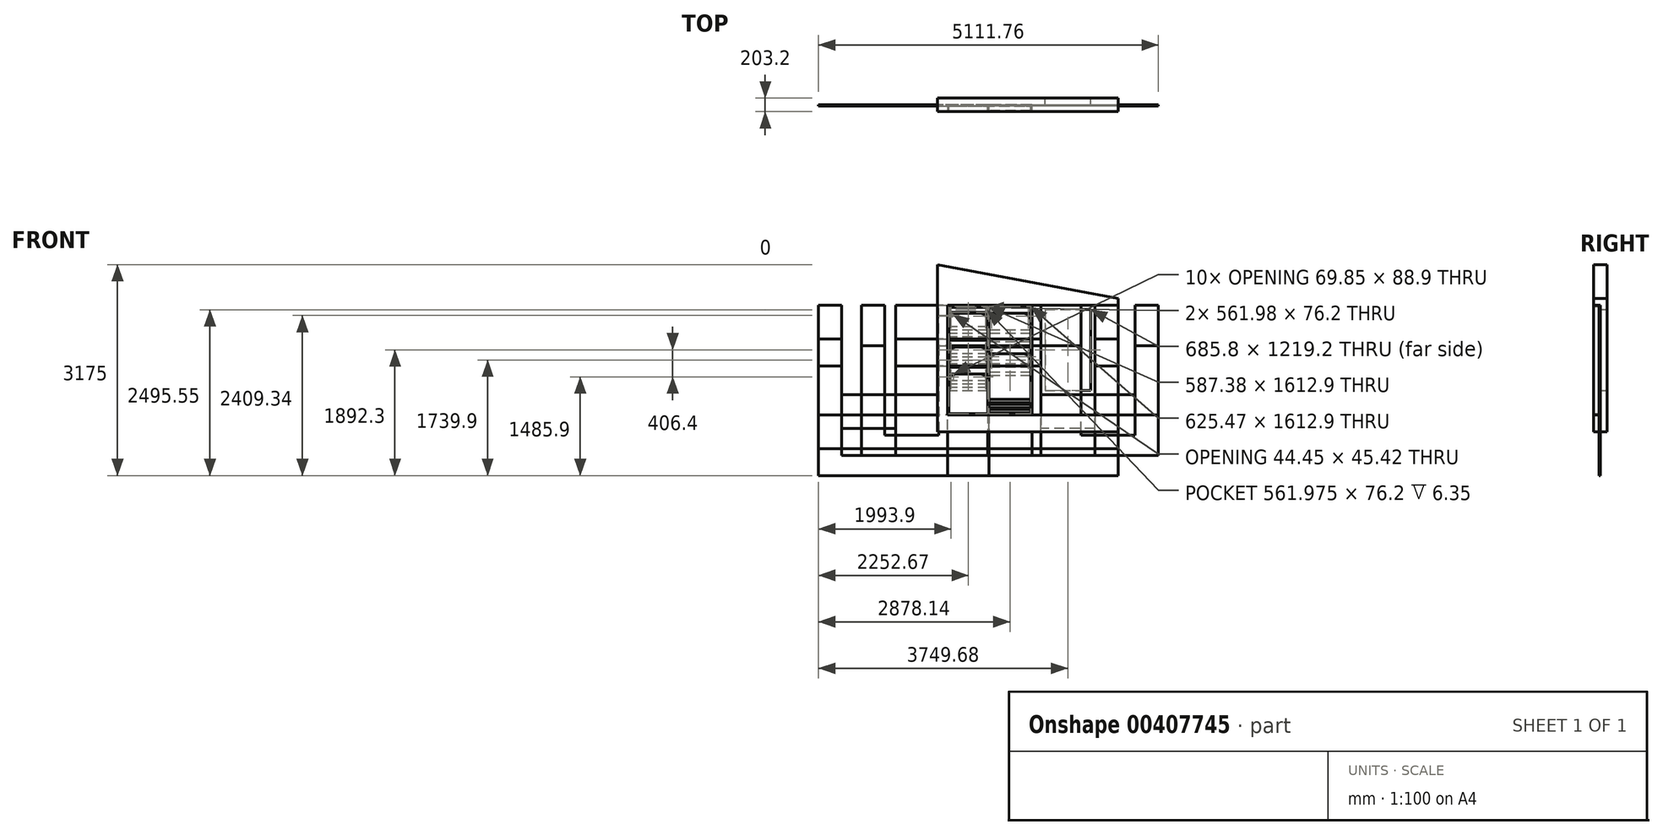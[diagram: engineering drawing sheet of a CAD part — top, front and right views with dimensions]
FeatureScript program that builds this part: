
annotation { "Feature Type Name" : "Feature", "Feature Type Description" : "" }
export const myFeature = defineFeature(function(context is Context, id is Id, definition is map)
    precondition{}
    {
        {
            var Q0;
            Q0=qCreatedBy(makeId("Front.planeOp"),FACE);
            var sketch = newSketch(context, id + "F0", { "sketchPlane" : qUnion([Q0])});
            skLineSegment(sketch, "E0.bottom", {"start": v(0, 0) * mm, "end": v(2717.8, 0) * mm});
            skLineSegment(sketch, "E0.top", {"start": v(0, 2006.6) * mm, "end": v(2717.8, 2006.6) * mm});
            skLineSegment(sketch, "E0.left", {"start": v(0, 0) * mm, "end": v(0, 2006.6) * mm});
            skLineSegment(sketch, "E0.right", {"start": v(2717.8, 0) * mm, "end": v(2717.8, 2006.6) * mm});
            skLineSegment(sketch, "E1.bottom", {"start": v(152.4, 254) * mm, "end": v(2717.8, 254) * mm});
            skLineSegment(sketch, "E1.top", {"start": v(152.4, 1905) * mm, "end": v(2717.8, 1905) * mm});
            skLineSegment(sketch, "E1.left", {"start": v(152.4, 254) * mm, "end": v(152.4, 1905) * mm});
            skLineSegment(sketch, "E1.right", {"start": v(2717.8, 254) * mm, "end": v(2717.8, 1905) * mm});
            skLineSegment(sketch, "E2", {"start": v(2717.8, 2006.6) * mm, "end": v(0, 2514.6) * mm});
            skLineSegment(sketch, "E3", {"start": v(0, 2514.6) * mm, "end": v(0, 2006.6) * mm});
            skSolve(sketch);
        }
        {
            var Q0;
            Q0=makeQuery(id+"F0.imprint","IMPRINT",FACE,{"disambiguationData":[TD([[makeQuery(id+"F0.imprint","IMPRINT",EDGE,{"derivedFrom":sQuery(id+"F0.wireOp",EDGE,"E0.bottom")}),1.0]])]});
            var Q1;
            Q1=makeQuery(id+"F0.imprint","IMPRINT",FACE,{"disambiguationData":[TD([[makeQuery(id+"F0.imprint","IMPRINT",EDGE,{"derivedFrom":sQuery(id+"F0.wireOp",EDGE,"E0.top")}),1.0]])]});
            var Q2;
            Q2=makeQuery(id+"F0.imprint","IMPRINT",FACE,{"disambiguationData":[TD([[makeQuery(id+"F0.imprint","IMPRINT",EDGE,{"derivedFrom":sQuery(id+"F0.wireOp",EDGE,"E1.bottom")}),1.0]])]});
            extrude(context, id + "F1", {"entities" : qUnion([Q0, Q1, Q2]), "oppositeDirection" : true, "depth" : 203.2 * mm});
        }
        {
            var Q0;
            Q0=makeQuery(id+"F0.imprint","IMPRINT",FACE,{"disambiguationData":[TD([[makeQuery(id+"F0.imprint","IMPRINT",EDGE,{"derivedFrom":sQuery(id+"F0.wireOp",EDGE,"E1.bottom")}),1.0]])]});
            extrude(context, id + "F2", {"entities" : qUnion([Q0]), "operationType" : NewBodyOperationType.REMOVE, "oppositeDirection" : true, "depth" : 101.6 * mm});
        }
        {
            var Q0;
            Q0=makeQuery(id+"F2.boolean.opBoolean","COPY",FACE,{"derivedFrom":makeQuery(id+"F2.opExtrude","CAP_FACE",FACE,{"disambiguationData":[OSD([sQuery(id+"F0.wireOp",EDGE,"E1.bottom"),sQuery(id+"F0.wireOp",EDGE,"E1.top"),sQuery(id+"F0.wireOp",EDGE,"E1.left"),sQuery(id+"F0.wireOp",EDGE,"E1.right")])],"isStart":false})});
            var sketch = newSketch(context, id + "F3", { "sketchPlane" : qUnion([Q0])});
            skLineSegment(sketch, "E4.bottom", {"start": v(1555.75, 1905) * mm, "end": v(2368.55, 1905) * mm});
            skLineSegment(sketch, "E4.top", {"start": v(1555.75, 558.8) * mm, "end": v(2368.55, 558.8) * mm});
            skLineSegment(sketch, "E4.left", {"start": v(1555.75, 1905) * mm, "end": v(1555.75, 558.8) * mm});
            skLineSegment(sketch, "E4.right", {"start": v(2368.55, 1905) * mm, "end": v(2368.55, 558.8) * mm});
            skLineSegment(sketch, "E5.0", {"start": v(1619.25, 1841.5) * mm, "end": v(1619.25, 622.3) * mm});
            skLineSegment(sketch, "E5.1", {"start": v(1619.25, 1841.5) * mm, "end": v(2305.05, 1841.5) * mm});
            skLineSegment(sketch, "E5.2", {"start": v(2305.05, 1841.5) * mm, "end": v(2305.05, 622.3) * mm});
            skLineSegment(sketch, "E5.3", {"start": v(1619.25, 622.3) * mm, "end": v(2305.05, 622.3) * mm});
            skSolve(sketch);
        }
        {
            var Q0;
            Q0=makeQuery(id+"F3.imprint","IMPRINT",FACE,{"disambiguationData":[TD([[makeQuery(id+"F3.imprint","IMPRINT",EDGE,{"derivedFrom":sQuery(id+"F3.wireOp",EDGE,"E4.bottom")}),-1.0]])]});
            extrude(context, id + "F4", {"entities" : qUnion([Q0]), "operationType" : NewBodyOperationType.ADD, "depth" : 12.7 * mm});
        }
        {
            var Q0;
            Q0=makeQuery(id+"F3.imprint","IMPRINT",FACE,{"disambiguationData":[TD([[makeQuery(id+"F3.imprint","IMPRINT",EDGE,{"derivedFrom":sQuery(id+"F3.wireOp",EDGE,"E5.0")}),1.0]])]});
            extrude(context, id + "F5", {"entities" : qUnion([Q0]), "operationType" : NewBodyOperationType.REMOVE, "endBound" : BoundingType.THROUGH_ALL, "oppositeDirection" : true, "depth" : 25.4 * mm});
        }
        {
            var Q0;
            {var subQ0=sQuery(id+"F0.wireOp",EDGE,"E1.left");var subQ1=sQuery(id+"F0.wireOp",EDGE,"E1.bottom");var subQ2=sQuery(id+"F0.wireOp",EDGE,"E1.top");var subQ3=sQuery(id+"F0.wireOp",EDGE,"E1.right");Q0=makeQuery(id+"F4.boolean.opBoolean","SPLIT",FACE,{"disambiguationData":[TD([makeQuery(id+"F2.boolean.opBoolean","COPY",FACE,{"derivedFrom":makeQuery(id+"F2.opExtrude","SWEPT_FACE",FACE,{"disambiguationData":[OSD([subQ1])]})})])],"derivedFrom":makeQuery(id+"F2.boolean.opBoolean","COPY",FACE,{"derivedFrom":makeQuery(id+"F2.opExtrude","CAP_FACE",FACE,{"disambiguationData":[OSD([subQ1,subQ2,subQ0,subQ3])],"isStart":false})})});}
            var sketch = newSketch(context, id + "F6", { "sketchPlane" : qUnion([Q0])});
            skLineSegment(sketch, "E6.bottom", {"start": v(152.4, 1905) * mm, "end": v(1422.4, 1905) * mm});
            skLineSegment(sketch, "E6.top", {"start": v(152.4, 254) * mm, "end": v(1422.4, 254) * mm});
            skLineSegment(sketch, "E6.left", {"start": v(152.4, 1905) * mm, "end": v(152.4, 254) * mm});
            skLineSegment(sketch, "E6.right", {"start": v(1422.4, 1905) * mm, "end": v(1422.4, 254) * mm});
            skLineSegment(sketch, "E7.bottom", {"start": v(171.45, 1885.95) * mm, "end": v(758.82, 1885.95) * mm});
            skLineSegment(sketch, "E7.top", {"start": v(171.45, 273.05) * mm, "end": v(758.82, 273.05) * mm});
            skLineSegment(sketch, "E7.left", {"start": v(171.45, 1885.95) * mm, "end": v(171.45, 273.05) * mm});
            skLineSegment(sketch, "E7.right", {"start": v(758.82, 1885.95) * mm, "end": v(758.82, 273.05) * mm});
            skLineSegment(sketch, "E8.bottom", {"start": v(777.87, 1885.95) * mm, "end": v(1403.35, 1885.95) * mm});
            skLineSegment(sketch, "E8.top", {"start": v(777.87, 273.05) * mm, "end": v(1403.35, 273.05) * mm});
            skLineSegment(sketch, "E8.left", {"start": v(777.87, 1885.95) * mm, "end": v(777.87, 273.05) * mm});
            skLineSegment(sketch, "E8.right", {"start": v(1403.35, 1885.95) * mm, "end": v(1403.35, 273.05) * mm});
            skSolve(sketch);
        }
        {
            var Q0;
            Q0=makeQuery(id+"F6.imprint","IMPRINT",FACE,{"disambiguationData":[TD([[makeQuery(id+"F6.imprint","IMPRINT",EDGE,{"derivedFrom":sQuery(id+"F6.wireOp",EDGE,"E6.bottom")}),-1.0]])]});
            extrude(context, id + "F7", {"entities" : qUnion([Q0]), "depth" : 101.6 * mm});
        }
        {
            var Q0;
            Q0=makeQuery(id+"F7.opExtrude","SWEPT_FACE",FACE,{"disambiguationData":[OSD([sQuery(id+"F6.wireOp",EDGE,"E7.left")])]});
            var sketch = newSketch(context, id + "F8", { "sketchPlane" : qUnion([Q0])});
            skLineSegment(sketch, "E9.bottom", {"start": v(101.6, 1885.95) * mm, "end": v(82.55, 1885.95) * mm});
            skLineSegment(sketch, "E9.top", {"start": v(101.6, 1784.35) * mm, "end": v(82.55, 1784.35) * mm});
            skLineSegment(sketch, "E9.left", {"start": v(101.6, 1885.95) * mm, "end": v(101.6, 1784.35) * mm});
            skLineSegment(sketch, "E9.right", {"start": v(82.55, 1885.95) * mm, "end": v(82.55, 1784.35) * mm});
            skSolve(sketch);
        }
        {
            var Q0;
            Q0=makeQuery(id+"F8.imprint","IMPRINT",FACE,{"disambiguationData":[TD([[makeQuery(id+"F8.imprint","IMPRINT",EDGE,{"derivedFrom":sQuery(id+"F8.wireOp",EDGE,"E9.bottom")}),-1.0]])]});
            extrude(context, id + "F9", {"entities" : qUnion([Q0]), "endBound" : BoundingType.UP_TO_NEXT, "depth" : 25.4 * mm});
        }
        {
            var Q0;
            Q0=makeQuery(id+"F9.opExtrude","SWEPT_BODY",BODY,{"disambiguationData":[OSD([sQuery(id+"F8.wireOp",EDGE,"E9.bottom"),sQuery(id+"F8.wireOp",EDGE,"E9.top"),sQuery(id+"F8.wireOp",EDGE,"E9.left"),sQuery(id+"F8.wireOp",EDGE,"E9.right")])]});
            transform(context, id + "F10", {"entities" : qUnion([Q0]), "transformType" : TransformType.TRANSLATION_3D, "dx" : 0 * mm, "dy" : 0 * mm, "dz" : -508 * mm, "makeCopy" : true});
        }
        {
            var Q0;
            Q0=makeQuery(id+"F10.opPattern","COPY",BODY,{"derivedFrom":makeQuery(id+"F9.opExtrude","SWEPT_BODY",BODY,{"disambiguationData":[OSD([sQuery(id+"F8.wireOp",EDGE,"E9.bottom"),sQuery(id+"F8.wireOp",EDGE,"E9.top"),sQuery(id+"F8.wireOp",EDGE,"E9.left"),sQuery(id+"F8.wireOp",EDGE,"E9.right")])]}),"instanceName":"1"});
            transform(context, id + "F11", {"entities" : qUnion([Q0]), "transformType" : TransformType.TRANSLATION_3D, "dx" : 0 * mm, "dy" : 0 * mm, "dz" : -406.4 * mm, "makeCopy" : true});
        }
        {
            var Q0;
            Q0=makeQuery(id+"F7.opExtrude","SWEPT_FACE",FACE,{"disambiguationData":[OSD([sQuery(id+"F6.wireOp",EDGE,"E8.left")])]});
            var sketch = newSketch(context, id + "F12", { "sketchPlane" : qUnion([Q0])});
            skLineSegment(sketch, "E10.bottom", {"start": v(101.6, 1885.95) * mm, "end": v(82.55, 1885.95) * mm});
            skLineSegment(sketch, "E10.top", {"start": v(101.6, 1784.35) * mm, "end": v(82.55, 1784.35) * mm});
            skLineSegment(sketch, "E10.left", {"start": v(101.6, 1885.95) * mm, "end": v(101.6, 1784.35) * mm});
            skLineSegment(sketch, "E10.right", {"start": v(82.55, 1885.95) * mm, "end": v(82.55, 1784.35) * mm});
            skLineSegment(sketch, "E11.0", {"start": v(101.6, 1784.35) * mm, "end": v(82.55, 1784.35) * mm, "construction": true});
            skSolve(sketch);
        }
        {
            var Q0;
            Q0=makeQuery(id+"F12.imprint","IMPRINT",FACE,{"disambiguationData":[TD([[makeQuery(id+"F12.imprint","IMPRINT",EDGE,{"derivedFrom":sQuery(id+"F12.wireOp",EDGE,"E10.bottom")}),-1.0]])]});
            extrude(context, id + "F13", {"entities" : qUnion([Q0]), "endBound" : BoundingType.UP_TO_NEXT, "depth" : 25.4 * mm});
        }
        {
            var Q0;
            Q0=makeQuery(id+"F13.opExtrude","SWEPT_BODY",BODY,{"disambiguationData":[OSD([sQuery(id+"F12.wireOp",EDGE,"E10.bottom"),sQuery(id+"F12.wireOp",EDGE,"E10.top"),sQuery(id+"F12.wireOp",EDGE,"E10.left"),sQuery(id+"F12.wireOp",EDGE,"E10.right")])]});
            transform(context, id + "F14", {"entities" : qUnion([Q0]), "transformType" : TransformType.TRANSLATION_3D, "dx" : 0 * mm, "dy" : 0 * mm, "dz" : -609.6 * mm, "makeCopy" : true});
        }
        {
            var Q0;
            Q0=makeQuery(id+"F7.opExtrude","SWEPT_FACE",FACE,{"disambiguationData":[OSD([sQuery(id+"F6.wireOp",EDGE,"E7.left")])]});
            var sketch = newSketch(context, id + "F15", { "sketchPlane" : qUnion([Q0])});
            skLineSegment(sketch, "E12.0", {"start": v(82.55, 1377.95) * mm, "end": v(101.6, 1377.95) * mm, "construction": true});
            skLineSegment(sketch, "E13.0", {"start": v(101.6, 1885.95) * mm, "end": v(101.6, 273.05) * mm, "construction": true});
            skLineSegment(sketch, "E14.bottom", {"start": v(101.6, 1428.75) * mm, "end": v(88.9, 1428.75) * mm});
            skLineSegment(sketch, "E14.top", {"start": v(101.6, 1479.55) * mm, "end": v(88.9, 1479.55) * mm});
            skLineSegment(sketch, "E14.left", {"start": v(101.6, 1428.75) * mm, "end": v(101.6, 1479.55) * mm});
            skLineSegment(sketch, "E14.right", {"start": v(88.9, 1428.75) * mm, "end": v(88.9, 1479.55) * mm});
            skSolve(sketch);
        }
        {
            var Q0;
            Q0=makeQuery(id+"F15.imprint","IMPRINT",FACE,{"disambiguationData":[TD([[makeQuery(id+"F15.imprint","IMPRINT",EDGE,{"derivedFrom":sQuery(id+"F15.wireOp",EDGE,"E14.bottom")}),-1.0]])]});
            extrude(context, id + "F16", {"entities" : qUnion([Q0]), "endBound" : BoundingType.UP_TO_NEXT, "depth" : 25.4 * mm});
        }
        {
            var Q0;
            Q0=makeQuery(id+"F16.opExtrude","SWEPT_BODY",BODY,{"disambiguationData":[OSD([sQuery(id+"F15.wireOp",EDGE,"E14.bottom"),sQuery(id+"F15.wireOp",EDGE,"E14.top"),sQuery(id+"F15.wireOp",EDGE,"E14.left"),sQuery(id+"F15.wireOp",EDGE,"E14.right")])]});
            transform(context, id + "F17", {"entities" : qUnion([Q0]), "transformType" : TransformType.TRANSLATION_3D, "dx" : 0 * mm, "dy" : 0 * mm, "dz" : 101.6 * mm, "makeCopy" : true});
        }
        {
            var Q0;
            Q0=makeQuery(id+"F16.opExtrude","SWEPT_BODY",BODY,{"disambiguationData":[OSD([sQuery(id+"F15.wireOp",EDGE,"E14.bottom"),sQuery(id+"F15.wireOp",EDGE,"E14.top"),sQuery(id+"F15.wireOp",EDGE,"E14.left"),sQuery(id+"F15.wireOp",EDGE,"E14.right")])]});
            transform(context, id + "F18", {"entities" : qUnion([Q0]), "transformType" : TransformType.TRANSLATION_3D, "dx" : 0 * mm, "dy" : 0 * mm, "dz" : -406.4 * mm, "makeCopy" : true});
        }
        {
            var Q0;
            Q0=makeQuery(id+"F18.opPattern","COPY",BODY,{"derivedFrom":makeQuery(id+"F16.opExtrude","SWEPT_BODY",BODY,{"disambiguationData":[OSD([sQuery(id+"F15.wireOp",EDGE,"E14.bottom"),sQuery(id+"F15.wireOp",EDGE,"E14.top"),sQuery(id+"F15.wireOp",EDGE,"E14.left"),sQuery(id+"F15.wireOp",EDGE,"E14.right")])]}),"instanceName":"1"});
            transform(context, id + "F19", {"entities" : qUnion([Q0]), "transformType" : TransformType.TRANSLATION_3D, "dx" : 0 * mm, "dy" : 0 * mm, "dz" : 101.6 * mm, "makeCopy" : true});
        }
        {
            var Q0;
            Q0=makeQuery(id+"F18.opPattern","COPY",BODY,{"derivedFrom":makeQuery(id+"F16.opExtrude","SWEPT_BODY",BODY,{"disambiguationData":[OSD([sQuery(id+"F15.wireOp",EDGE,"E14.bottom"),sQuery(id+"F15.wireOp",EDGE,"E14.top"),sQuery(id+"F15.wireOp",EDGE,"E14.left"),sQuery(id+"F15.wireOp",EDGE,"E14.right")])]}),"instanceName":"1"});
            transform(context, id + "F20", {"entities" : qUnion([Q0]), "transformType" : TransformType.TRANSLATION_3D, "dx" : 0 * mm, "dy" : 0 * mm, "dz" : -406.4 * mm, "makeCopy" : true});
        }
        {
            var Q0;
            Q0=makeQuery(id+"F20.opPattern","COPY",BODY,{"derivedFrom":makeQuery(id+"F18.opPattern","COPY",BODY,{"derivedFrom":makeQuery(id+"F16.opExtrude","SWEPT_BODY",BODY,{"disambiguationData":[OSD([sQuery(id+"F15.wireOp",EDGE,"E14.bottom"),sQuery(id+"F15.wireOp",EDGE,"E14.top"),sQuery(id+"F15.wireOp",EDGE,"E14.left"),sQuery(id+"F15.wireOp",EDGE,"E14.right")])]}),"instanceName":"1"}),"instanceName":"1"});
            transform(context, id + "F21", {"entities" : qUnion([Q0]), "transformType" : TransformType.TRANSLATION_3D, "dx" : 0 * mm, "dy" : 0 * mm, "dz" : 101.6 * mm, "makeCopy" : true});
        }
        {
            var Q0;
            Q0=makeQuery(id+"F7.opExtrude","SWEPT_FACE",FACE,{"disambiguationData":[OSD([sQuery(id+"F6.wireOp",EDGE,"E8.left")])]});
            var sketch = newSketch(context, id + "F22", { "sketchPlane" : qUnion([Q0])});
            skLineSegment(sketch, "E15.0", {"start": v(82.55, 1276.35) * mm, "end": v(101.6, 1276.35) * mm, "construction": true});
            skLineSegment(sketch, "E16.0", {"start": v(101.6, 1885.95) * mm, "end": v(101.6, 273.05) * mm, "construction": true});
            skLineSegment(sketch, "E17.bottom", {"start": v(101.6, 1352.55) * mm, "end": v(88.9, 1352.55) * mm});
            skLineSegment(sketch, "E17.top", {"start": v(101.6, 1403.35) * mm, "end": v(88.9, 1403.35) * mm});
            skLineSegment(sketch, "E17.left", {"start": v(101.6, 1352.55) * mm, "end": v(101.6, 1403.35) * mm});
            skLineSegment(sketch, "E17.right", {"start": v(88.9, 1352.55) * mm, "end": v(88.9, 1403.35) * mm});
            skSolve(sketch);
        }
        {
            var Q0;
            Q0=makeQuery(id+"F22.imprint","IMPRINT",FACE,{"disambiguationData":[TD([[makeQuery(id+"F22.imprint","IMPRINT",EDGE,{"derivedFrom":sQuery(id+"F22.wireOp",EDGE,"E17.bottom")}),-1.0]])]});
            extrude(context, id + "F23", {"entities" : qUnion([Q0]), "endBound" : BoundingType.UP_TO_NEXT, "depth" : 25.4 * mm});
        }
        {
            var Q0;
            Q0=makeQuery(id+"F23.opExtrude","SWEPT_BODY",BODY,{"disambiguationData":[OSD([sQuery(id+"F22.wireOp",EDGE,"E17.bottom"),sQuery(id+"F22.wireOp",EDGE,"E17.top"),sQuery(id+"F22.wireOp",EDGE,"E17.left"),sQuery(id+"F22.wireOp",EDGE,"E17.right")])]});
            transform(context, id + "F24", {"entities" : qUnion([Q0]), "transformType" : TransformType.TRANSLATION_3D, "dx" : 0 * mm, "dy" : 0 * mm, "dz" : 127 * mm, "makeCopy" : true});
        }
        {
            var Q0;
            Q0=makeQuery(id+"F23.opExtrude","SWEPT_BODY",BODY,{"disambiguationData":[OSD([sQuery(id+"F22.wireOp",EDGE,"E17.bottom"),sQuery(id+"F22.wireOp",EDGE,"E17.top"),sQuery(id+"F22.wireOp",EDGE,"E17.left"),sQuery(id+"F22.wireOp",EDGE,"E17.right")])]});
            transform(context, id + "F25", {"entities" : qUnion([Q0]), "transformType" : TransformType.TRANSLATION_3D, "dx" : 0 * mm, "dy" : 0 * mm, "dz" : -508 * mm, "makeCopy" : true});
        }
        {
            var Q0;
            Q0=makeQuery(id+"F25.opPattern","COPY",BODY,{"derivedFrom":makeQuery(id+"F23.opExtrude","SWEPT_BODY",BODY,{"disambiguationData":[OSD([sQuery(id+"F22.wireOp",EDGE,"E17.bottom"),sQuery(id+"F22.wireOp",EDGE,"E17.top"),sQuery(id+"F22.wireOp",EDGE,"E17.left"),sQuery(id+"F22.wireOp",EDGE,"E17.right")])]}),"instanceName":"1"});
            transform(context, id + "F26", {"entities" : qUnion([Q0]), "transformType" : TransformType.TRANSLATION_3D, "dx" : 0 * mm, "dy" : 0 * mm, "dz" : 127 * mm, "makeCopy" : true});
        }
        {
            var Q0;
            Q0=makeQuery(id+"F7.opExtrude","SWEPT_FACE",FACE,{"disambiguationData":[OSD([sQuery(id+"F6.wireOp",EDGE,"E8.left")])]});
            var sketch = newSketch(context, id + "F27", { "sketchPlane" : qUnion([Q0])});
            skLineSegment(sketch, "E18.0", {"start": v(0, 273.05) * mm, "end": v(101.6, 273.05) * mm, "construction": true});
            skLineSegment(sketch, "E19.0", {"start": v(0, 1885.95) * mm, "end": v(0, 273.05) * mm, "construction": true});
            skLineSegment(sketch, "E20.bottom", {"start": v(0, 285.75) * mm, "end": v(12.7, 285.75) * mm});
            skLineSegment(sketch, "E20.top", {"start": v(0, 336.55) * mm, "end": v(12.7, 336.55) * mm});
            skLineSegment(sketch, "E20.left", {"start": v(0, 285.75) * mm, "end": v(0, 336.55) * mm});
            skLineSegment(sketch, "E20.right", {"start": v(12.7, 285.75) * mm, "end": v(12.7, 336.55) * mm});
            skSolve(sketch);
        }
        {
            var Q0;
            Q0=makeQuery(id+"F27.imprint","IMPRINT",FACE,{"disambiguationData":[TD([[makeQuery(id+"F27.imprint","IMPRINT",EDGE,{"derivedFrom":sQuery(id+"F27.wireOp",EDGE,"E20.bottom")}),1.0]])]});
            extrude(context, id + "F28", {"entities" : qUnion([Q0]), "endBound" : BoundingType.UP_TO_NEXT, "depth" : 25.4 * mm});
        }
        {
            var Q0;
            Q0=makeQuery(id+"F28.opExtrude","SWEPT_BODY",BODY,{"disambiguationData":[OSD([sQuery(id+"F27.wireOp",EDGE,"E20.bottom"),sQuery(id+"F27.wireOp",EDGE,"E20.top"),sQuery(id+"F27.wireOp",EDGE,"E20.left"),sQuery(id+"F27.wireOp",EDGE,"E20.right")])]});
            transform(context, id + "F29", {"entities" : qUnion([Q0]), "transformType" : TransformType.TRANSLATION_3D, "dx" : 0 * mm, "dy" : 0 * mm, "dz" : 76.2 * mm, "makeCopy" : true});
        }
        {
            var Q0;
            Q0=makeQuery(id+"F29.opPattern","COPY",BODY,{"derivedFrom":makeQuery(id+"F28.opExtrude","SWEPT_BODY",BODY,{"disambiguationData":[OSD([sQuery(id+"F27.wireOp",EDGE,"E20.bottom"),sQuery(id+"F27.wireOp",EDGE,"E20.top"),sQuery(id+"F27.wireOp",EDGE,"E20.left"),sQuery(id+"F27.wireOp",EDGE,"E20.right")])]}),"instanceName":"1"});
            transform(context, id + "F30", {"entities" : qUnion([Q0]), "transformType" : TransformType.TRANSLATION_3D, "dx" : 0 * mm, "dy" : 0 * mm, "dz" : 76.2 * mm, "makeCopy" : true});
        }
        {
            var Q0;
            {var subQ0=sQuery(id+"F0.wireOp",EDGE,"E1.left");var subQ1=sQuery(id+"F0.wireOp",EDGE,"E1.bottom");var subQ2=sQuery(id+"F0.wireOp",EDGE,"E1.top");var subQ3=sQuery(id+"F0.wireOp",EDGE,"E1.right");Q0=makeQuery(id+"F4.boolean.opBoolean","SPLIT",FACE,{"disambiguationData":[TD([makeQuery(id+"F2.boolean.opBoolean","COPY",FACE,{"derivedFrom":makeQuery(id+"F2.opExtrude","SWEPT_FACE",FACE,{"disambiguationData":[OSD([subQ1])]})})])],"derivedFrom":makeQuery(id+"F2.boolean.opBoolean","COPY",FACE,{"derivedFrom":makeQuery(id+"F2.opExtrude","CAP_FACE",FACE,{"disambiguationData":[OSD([subQ1,subQ2,subQ0,subQ3])],"isStart":false})})});}
            var sketch = newSketch(context, id + "F31", { "sketchPlane" : qUnion([Q0])});
            skLineSegment(sketch, "E21.0", {"start": v(171.45, 1885.95) * mm, "end": v(171.45, 273.05) * mm, "construction": true});
            skLineSegment(sketch, "E22.0", {"start": v(758.83, 1784.35) * mm, "end": v(171.45, 1784.35) * mm, "construction": true});
            skArc(sketch, "E23", {"start": v(190.5, 1695.45) * mm, "mid": v(204.76, 1736.1) * mm, "end": v(241.3, 1758.95) * mm});
            skLineSegment(sketch, "E24", {"start": v(190.5, 1695.45) * mm, "end": v(171.45, 1695.45) * mm});
            skLineSegment(sketch, "E25", {"start": v(171.45, 1695.45) * mm, "end": v(171.45, 1784.35) * mm});
            skLineSegment(sketch, "E26", {"start": v(171.45, 1784.35) * mm, "end": v(241.3, 1784.35) * mm});
            skLineSegment(sketch, "E27", {"start": v(241.3, 1784.35) * mm, "end": v(241.3, 1758.95) * mm});
            skLineSegment(sketch, "E28", {"start": v(190.5, 1695.45) * mm, "end": v(190.5, 1784.35) * mm, "construction": true});
            skLineSegment(sketch, "E29", {"start": v(241.3, 1758.95) * mm, "end": v(171.45, 1743.23) * mm, "construction": true});
            skSolve(sketch);
        }
        {
            var Q0;
            Q0=makeQuery(id+"F31.imprint","IMPRINT",FACE,{"disambiguationData":[TD([[makeQuery(id+"F31.imprint","IMPRINT",EDGE,{"derivedFrom":sQuery(id+"F31.wireOp",EDGE,"E23")}),1.0]])]});
            var Q1;
            Q1=makeQuery(id+"F9.opExtrude","SWEPT_FACE",FACE,{"disambiguationData":[OSD([sQuery(id+"F8.wireOp",EDGE,"E9.right")])]});
            extrude(context, id + "F32", {"entities" : qUnion([Q0]), "endBound" : BoundingType.UP_TO_SURFACE, "endBoundEntityFace" : qUnion([Q1]), "depth" : 25.4 * mm});
        }
        {
            var Q0;
            Q0=makeQuery(id+"F32.opExtrude","SWEPT_BODY",BODY,{"disambiguationData":[OSD([sQuery(id+"F31.wireOp",EDGE,"E23"),sQuery(id+"F31.wireOp",EDGE,"E24"),sQuery(id+"F31.wireOp",EDGE,"E25"),sQuery(id+"F31.wireOp",EDGE,"E26"),sQuery(id+"F31.wireOp",EDGE,"E27")])]});
            transform(context, id + "F33", {"entities" : qUnion([Q0]), "transformType" : TransformType.TRANSLATION_3D, "dx" : 0 * mm, "dy" : 0 * mm, "dz" : -508 * mm, "makeCopy" : true});
        }
        {
            var Q0;
            Q0=makeQuery(id+"F33.opPattern","COPY",BODY,{"derivedFrom":makeQuery(id+"F32.opExtrude","SWEPT_BODY",BODY,{"disambiguationData":[OSD([sQuery(id+"F31.wireOp",EDGE,"E23"),sQuery(id+"F31.wireOp",EDGE,"E24"),sQuery(id+"F31.wireOp",EDGE,"E25"),sQuery(id+"F31.wireOp",EDGE,"E26"),sQuery(id+"F31.wireOp",EDGE,"E27")])]}),"instanceName":"1"});
            transform(context, id + "F34", {"entities" : qUnion([Q0]), "transformType" : TransformType.TRANSLATION_3D, "dx" : 0 * mm, "dy" : 0 * mm, "dz" : -406.4 * mm, "makeCopy" : true});
        }
        {
            var Q0;
            Q0=makeQuery(id+"F7.opExtrude","SWEPT_FACE",FACE,{"disambiguationData":[OSD([sQuery(id+"F6.wireOp",EDGE,"E7.left")])]});
            var Q1;
            Q1=makeQuery(id+"F7.opExtrude","SWEPT_FACE",FACE,{"disambiguationData":[OSD([sQuery(id+"F6.wireOp",EDGE,"E7.right")])]});
            cPlane(context, id + "F35", {"entities" : qUnion([Q0, Q1]), "cplaneType" : CPlaneType.MID_PLANE, "offset" : 25.4 * mm, "width" : 152.4 * mm, "height" : 152.4 * mm});
        }
        {
            var Q0;
            Q0=makeQuery(id+"F32.opExtrude","SWEPT_BODY",BODY,{"disambiguationData":[OSD([sQuery(id+"F31.wireOp",EDGE,"E23"),sQuery(id+"F31.wireOp",EDGE,"E24"),sQuery(id+"F31.wireOp",EDGE,"E25"),sQuery(id+"F31.wireOp",EDGE,"E26"),sQuery(id+"F31.wireOp",EDGE,"E27")])]});
            var Q1;
            Q1=makeQuery(id+"F33.opPattern","COPY",BODY,{"derivedFrom":makeQuery(id+"F32.opExtrude","SWEPT_BODY",BODY,{"disambiguationData":[OSD([sQuery(id+"F31.wireOp",EDGE,"E23"),sQuery(id+"F31.wireOp",EDGE,"E24"),sQuery(id+"F31.wireOp",EDGE,"E25"),sQuery(id+"F31.wireOp",EDGE,"E26"),sQuery(id+"F31.wireOp",EDGE,"E27")])]}),"instanceName":"1"});
            var Q2;
            Q2=makeQuery(id+"F34.opPattern","COPY",BODY,{"derivedFrom":makeQuery(id+"F33.opPattern","COPY",BODY,{"derivedFrom":makeQuery(id+"F32.opExtrude","SWEPT_BODY",BODY,{"disambiguationData":[OSD([sQuery(id+"F31.wireOp",EDGE,"E23"),sQuery(id+"F31.wireOp",EDGE,"E24"),sQuery(id+"F31.wireOp",EDGE,"E25"),sQuery(id+"F31.wireOp",EDGE,"E26"),sQuery(id+"F31.wireOp",EDGE,"E27")])]}),"instanceName":"1"}),"instanceName":"1"});
            var Q3;
            Q3=qCreatedBy(id+"F35.planeOp",FACE);
            mirror(context, id + "F36", {"entities" : qUnion([Q0, Q1, Q2]), "mirrorPlane" : qUnion([Q3])});
        }
        {
            var Q0;
            Q0=makeQuery(id+"F32.opExtrude","SWEPT_BODY",BODY,{"disambiguationData":[OSD([sQuery(id+"F31.wireOp",EDGE,"E23"),sQuery(id+"F31.wireOp",EDGE,"E24"),sQuery(id+"F31.wireOp",EDGE,"E25"),sQuery(id+"F31.wireOp",EDGE,"E26"),sQuery(id+"F31.wireOp",EDGE,"E27")])]});
            transform(context, id + "F37", {"entities" : qUnion([Q0]), "transformType" : TransformType.TRANSLATION_3D, "dx" : 606.42 * mm, "dy" : 0 * mm, "dz" : 0 * mm, "makeCopy" : true});
        }
        {
            var Q0;
            Q0=makeQuery(id+"F37.opPattern","COPY",BODY,{"derivedFrom":makeQuery(id+"F32.opExtrude","SWEPT_BODY",BODY,{"disambiguationData":[OSD([sQuery(id+"F31.wireOp",EDGE,"E23"),sQuery(id+"F31.wireOp",EDGE,"E24"),sQuery(id+"F31.wireOp",EDGE,"E25"),sQuery(id+"F31.wireOp",EDGE,"E26"),sQuery(id+"F31.wireOp",EDGE,"E27")])]}),"instanceName":"1"});
            transform(context, id + "F38", {"entities" : qUnion([Q0]), "transformType" : TransformType.TRANSLATION_3D, "dx" : 0 * mm, "dy" : 0 * mm, "dz" : -609.6 * mm, "makeCopy" : true});
        }
        {
            var Q0;
            Q0=makeQuery(id+"F7.opExtrude","SWEPT_FACE",FACE,{"disambiguationData":[OSD([sQuery(id+"F6.wireOp",EDGE,"E8.left")])]});
            var Q1;
            Q1=makeQuery(id+"F7.opExtrude","SWEPT_FACE",FACE,{"disambiguationData":[OSD([sQuery(id+"F6.wireOp",EDGE,"E8.right")])]});
            cPlane(context, id + "F39", {"entities" : qUnion([Q0, Q1]), "cplaneType" : CPlaneType.MID_PLANE, "offset" : 25.4 * mm, "width" : 152.4 * mm, "height" : 152.4 * mm});
        }
        {
            var Q0;
            Q0=makeQuery(id+"F37.opPattern","COPY",BODY,{"derivedFrom":makeQuery(id+"F32.opExtrude","SWEPT_BODY",BODY,{"disambiguationData":[OSD([sQuery(id+"F31.wireOp",EDGE,"E23"),sQuery(id+"F31.wireOp",EDGE,"E24"),sQuery(id+"F31.wireOp",EDGE,"E25"),sQuery(id+"F31.wireOp",EDGE,"E26"),sQuery(id+"F31.wireOp",EDGE,"E27")])]}),"instanceName":"1"});
            var Q1;
            Q1=makeQuery(id+"F38.opPattern","COPY",BODY,{"derivedFrom":makeQuery(id+"F37.opPattern","COPY",BODY,{"derivedFrom":makeQuery(id+"F32.opExtrude","SWEPT_BODY",BODY,{"disambiguationData":[OSD([sQuery(id+"F31.wireOp",EDGE,"E23"),sQuery(id+"F31.wireOp",EDGE,"E24"),sQuery(id+"F31.wireOp",EDGE,"E25"),sQuery(id+"F31.wireOp",EDGE,"E26"),sQuery(id+"F31.wireOp",EDGE,"E27")])]}),"instanceName":"1"}),"instanceName":"1"});
            var Q2;
            Q2=qCreatedBy(id+"F39.planeOp",FACE);
            mirror(context, id + "F40", {"entities" : qUnion([Q0, Q1]), "mirrorPlane" : qUnion([Q2])});
        }
        {
            var Q0;
            Q0=makeQuery(id+"F9.opExtrude","SWEPT_FACE",FACE,{"disambiguationData":[OSD([sQuery(id+"F8.wireOp",EDGE,"E9.right")])]});
            var sketch = newSketch(context, id + "F41", { "sketchPlane" : qUnion([Q0])});
            skLineSegment(sketch, "E30.0.0", {"start": v(758.82, 1784.35) * mm, "end": v(758.82, 1885.95) * mm, "construction": true});
            skLineSegment(sketch, "E30.0.1", {"start": v(758.83, 1885.95) * mm, "end": v(171.45, 1885.95) * mm, "construction": true});
            skLineSegment(sketch, "E30.0.2", {"start": v(171.45, 1885.95) * mm, "end": v(171.45, 1784.35) * mm, "construction": true});
            skLineSegment(sketch, "E30.0.3", {"start": v(171.45, 1784.35) * mm, "end": v(758.83, 1784.35) * mm, "construction": true});
            skLineSegment(sketch, "E31.0", {"start": v(184.15, 1873.25) * mm, "end": v(184.15, 1797.05) * mm});
            skLineSegment(sketch, "E31.1", {"start": v(746.13, 1873.25) * mm, "end": v(184.15, 1873.25) * mm});
            skLineSegment(sketch, "E31.2", {"start": v(746.13, 1797.05) * mm, "end": v(746.13, 1873.25) * mm});
            skLineSegment(sketch, "E31.3", {"start": v(184.15, 1797.05) * mm, "end": v(746.13, 1797.05) * mm});
            skSolve(sketch);
        }
        {
            var Q0;
            Q0=makeQuery(id+"F41.imprint","IMPRINT",FACE,{"disambiguationData":[TD([[makeQuery(id+"F41.imprint","IMPRINT",EDGE,{"derivedFrom":sQuery(id+"F41.wireOp",EDGE,"E31.0")}),1.0]])]});
            extrude(context, id + "F42", {"entities" : qUnion([Q0]), "operationType" : NewBodyOperationType.REMOVE, "oppositeDirection" : true, "depth" : 6.35 * mm, "offsetDistance" : 25.4 * mm});
        }
        {
            var Q0;
            Q0=makeQuery(id+"F32.opExtrude","CAP_FACE",FACE,{"disambiguationData":[OSD([sQuery(id+"F31.wireOp",EDGE,"E23"),sQuery(id+"F31.wireOp",EDGE,"E24"),sQuery(id+"F31.wireOp",EDGE,"E25"),sQuery(id+"F31.wireOp",EDGE,"E26"),sQuery(id+"F31.wireOp",EDGE,"E27")])],"isStart":false});
            var sketch = newSketch(context, id + "F43", { "sketchPlane" : qUnion([Q0])});
            skLineSegment(sketch, "E32.0.0", {"start": v(241.3, 1758.95) * mm, "end": v(241.3, 1784.35) * mm});
            skLineSegment(sketch, "E32.0.1", {"start": v(241.3, 1784.35) * mm, "end": v(171.45, 1784.35) * mm});
            skLineSegment(sketch, "E32.0.2", {"start": v(171.45, 1784.35) * mm, "end": v(171.45, 1695.45) * mm});
            skLineSegment(sketch, "E32.0.3", {"start": v(171.45, 1695.45) * mm, "end": v(190.5, 1695.45) * mm});
            skArc(sketch, "E32.0.4", {"start": v(241.3, 1758.95) * mm, "mid": v(204.76, 1736.1) * mm, "end": v(190.5, 1695.45) * mm});
            skLineSegment(sketch, "E33.0", {"start": v(184.15, 1771.65) * mm, "end": v(184.15, 1708.15) * mm});
            skLineSegment(sketch, "E33.1", {"start": v(228.6, 1771.65) * mm, "end": v(184.15, 1771.65) * mm});
            skLineSegment(sketch, "E33.2", {"start": v(178.84, 1708.15) * mm, "end": v(184.15, 1708.15) * mm});
            skArc(sketch, "E33.3", {"start": v(228.6, 1768.4) * mm, "mid": v(195.6, 1744.98) * mm, "end": v(178.84, 1708.15) * mm});
            skLineSegment(sketch, "E33.4", {"start": v(228.6, 1768.4) * mm, "end": v(228.6, 1771.65) * mm});
            skSolve(sketch);
        }
        {
            var Q0;
            {var subQ0=sQuery(id+"F43.wireOp",EDGE,"E33.1");Q0=makeQuery(id+"F43.imprint","IMPRINT",FACE,{"disambiguationData":[TD([[makeQuery(id+"F43.imprint","IMPRINT",EDGE,{"derivedFrom":subQ0}),1.0]])]});}
            extrude(context, id + "F44", {"entities" : qUnion([Q0]), "operationType" : NewBodyOperationType.REMOVE, "oppositeDirection" : true, "depth" : 6.35 * mm, "offsetDistance" : 25.4 * mm});
        }
    });
